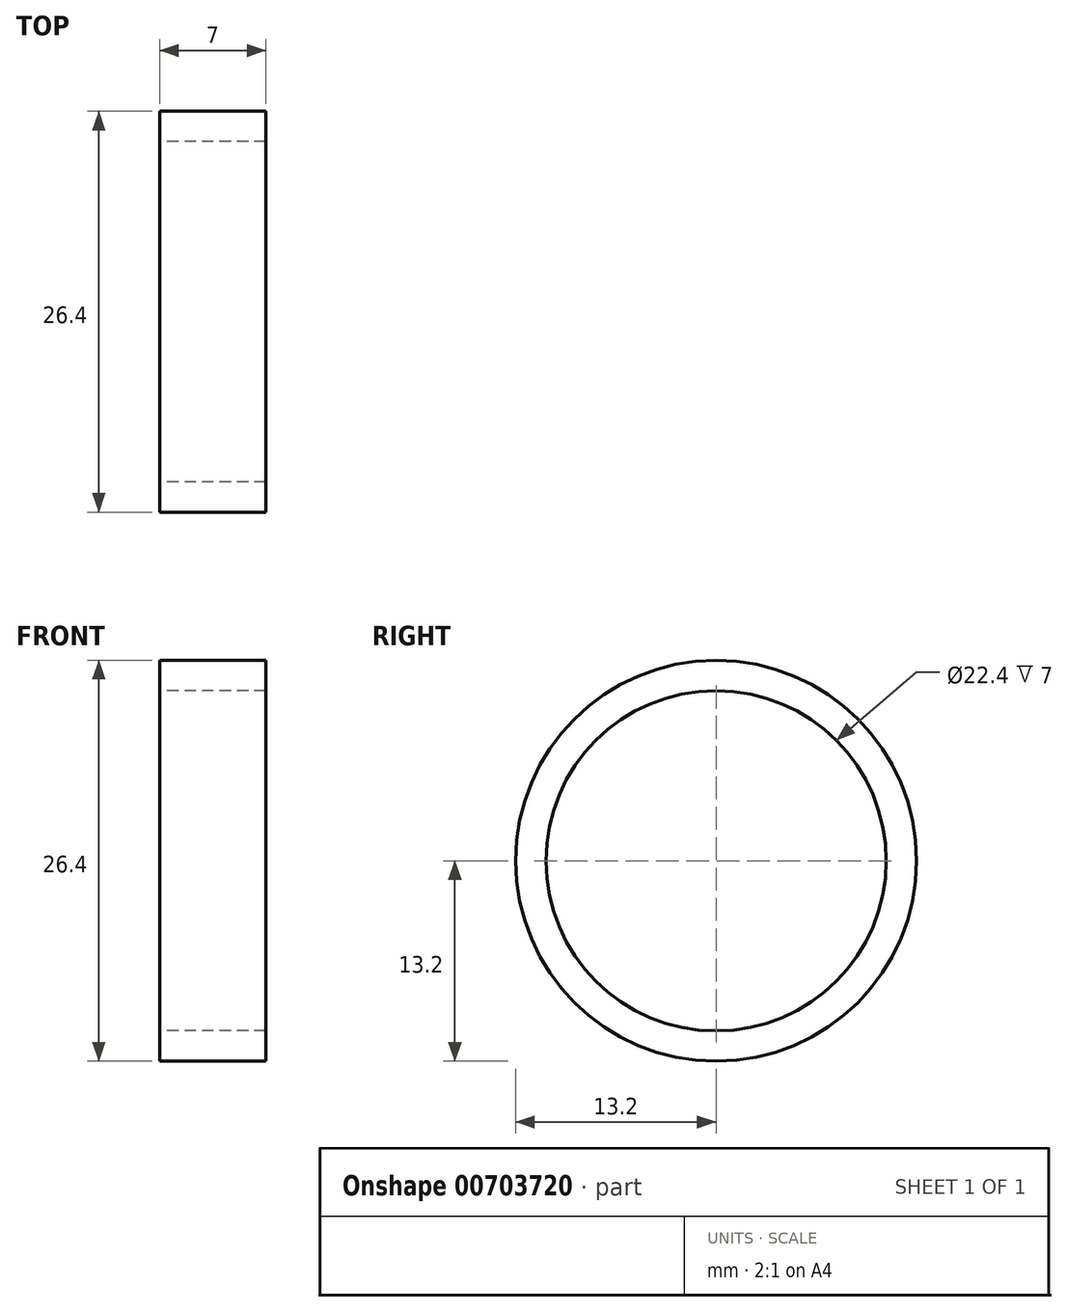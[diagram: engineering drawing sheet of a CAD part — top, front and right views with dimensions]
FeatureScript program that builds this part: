
annotation { "Feature Type Name" : "Feature", "Feature Type Description" : "" }
export const myFeature = defineFeature(function(context is Context, id is Id, definition is map)
    precondition{}
    {
        {
            var Q0;
            Q0=qCreatedBy(makeId("Right.planeOp"),FACE);
            var sketch = newSketch(context, id + "F0", { "sketchPlane" : qUnion([Q0])});
            skCircle(sketch, "E0", {"center": v(0, 0) * mm, "radius": 11.2 * mm});
            skCircle(sketch, "E1", {"center": v(0, 0) * mm, "radius": 13.2 * mm});
            skSolve(sketch);
        }
        {
            var Q0;
            Q0=makeQuery(id+"F0.imprint","IMPRINT",FACE,{"disambiguationData":[TD([[makeQuery(id+"F0.imprint","IMPRINT",EDGE,{"derivedFrom":sQuery(id+"F0.wireOp",EDGE,"E0")}),-1.0]])]});
            extrude(context, id + "F1", {"entities" : qUnion([Q0]), "depth" : 7 * mm, "offsetDistance" : 25 * mm});
        }
    });
